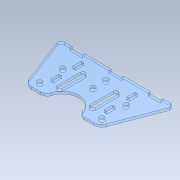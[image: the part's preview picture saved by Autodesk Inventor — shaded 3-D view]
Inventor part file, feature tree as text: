
AUTODESK INVENTOR PART (.ipt)
format: ipt  version: 2022 (Build 260153000, 153)  size: 344,576 bytes
history: native  units: mm
features: extrude x1, sketch x1
ambient origin geometry x8: Origin, YZ Plane, XZ Plane, XY Plane, X Axis, Y Axis, Z Axis, Center Point
bodies: Body1 (feature_tree)
feature tree (2):
  extrude  "Extrusion2"  [1 undecoded]
  sketch  "Sketch2"  dims[d3=3.0mm d4=0.0mm]
note: 1 required parameter value undecoded (feature->parameter linkage not recoverable at this tier; creation-order binding heuristic only, values carry confidence <= 0.55)
